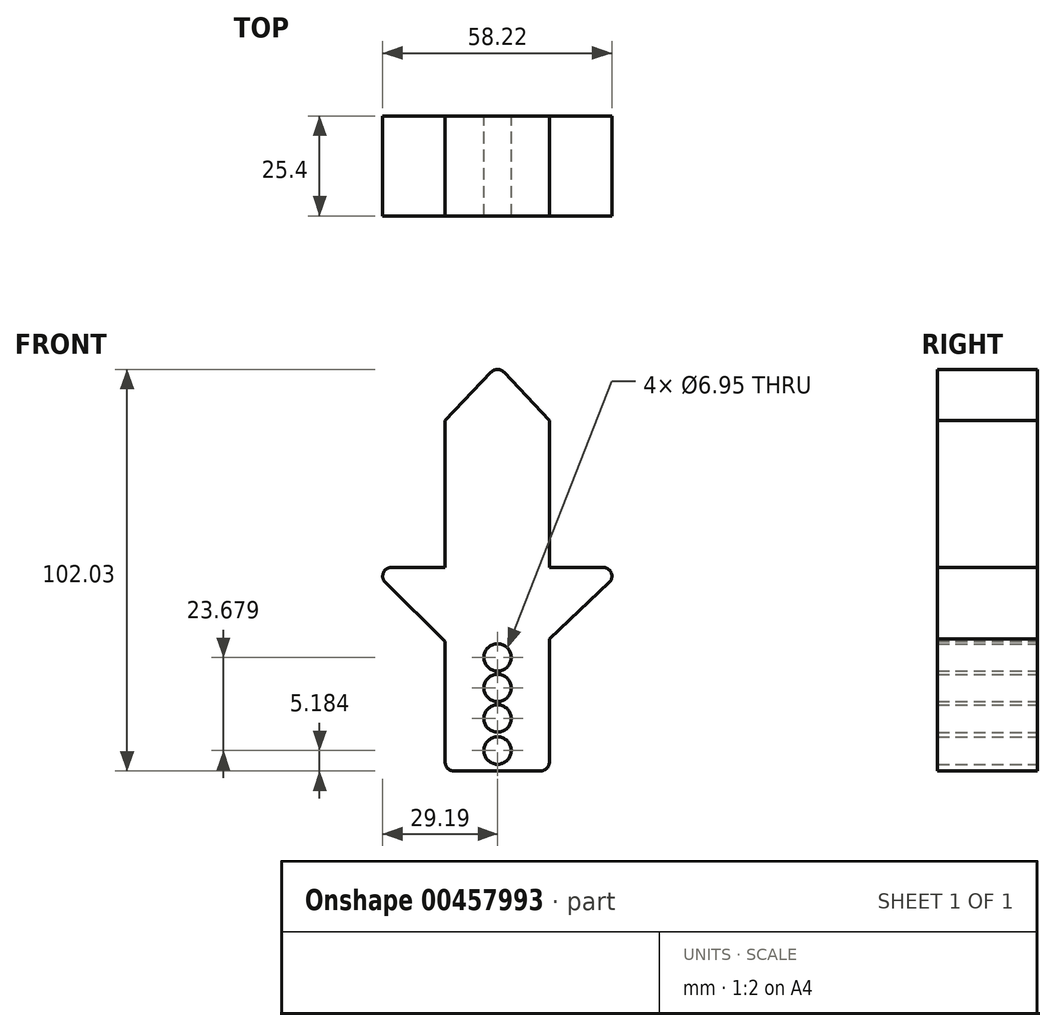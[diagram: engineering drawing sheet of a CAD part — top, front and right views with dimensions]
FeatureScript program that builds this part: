
annotation { "Feature Type Name" : "Feature", "Feature Type Description" : "" }
export const myFeature = defineFeature(function(context is Context, id is Id, definition is map)
    precondition{}
    {
        {
            var Q0;
            Q0=qCreatedBy(makeId("Front.planeOp"),FACE);
            var sketch = newSketch(context, id + "F0", { "sketchPlane" : qUnion([Q0])});
            skLineSegment(sketch, "E0", {"start": v(-13.32, 0) * mm, "end": v(-13.32, 37.28) * mm});
            skLineSegment(sketch, "E1", {"start": v(13.13, 37.28) * mm, "end": v(13.13, 0) * mm});
            skLineSegment(sketch, "E2", {"start": v(-13.32, 37.28) * mm, "end": v(0, 51.34) * mm});
            skLineSegment(sketch, "E3", {"start": v(13.13, 37.28) * mm, "end": v(0, 51.34) * mm});
            skLineSegment(sketch, "E4", {"start": v(-13.32, 0) * mm, "end": v(-32.37, 0) * mm});
            skLineSegment(sketch, "E5", {"start": v(-32.37, 0) * mm, "end": v(-13.32, -18.78) * mm});
            skLineSegment(sketch, "E6", {"start": v(13.13, 0) * mm, "end": v(32.37, 0) * mm});
            skLineSegment(sketch, "E7", {"start": v(32.37, 0) * mm, "end": v(13.13, -18.22) * mm});
            skLineSegment(sketch, "E8", {"start": v(-13.32, -18.78) * mm, "end": v(-13.32, -51.7) * mm});
            skLineSegment(sketch, "E9", {"start": v(-13.32, -51.7) * mm, "end": v(13.13, -51.7) * mm});
            skLineSegment(sketch, "E10", {"start": v(13.13, -18.22) * mm, "end": v(13.13, -51.7) * mm});
            skSolve(sketch);
        }
        {
            var Q0;
            Q0=makeQuery(id+"F0.imprint","IMPRINT",FACE,{"disambiguationData":[TD([[makeQuery(id+"F0.imprint","IMPRINT",EDGE,{"derivedFrom":sQuery(id+"F0.wireOp",EDGE,"E0")}),-1.0]])]});
            extrude(context, id + "F1", {"entities" : qUnion([Q0]), "depth" : 25.4 * mm});
        }
        {
            var Q0;
            Q0=qCreatedBy(makeId("Front.planeOp"),FACE);
            var sketch = newSketch(context, id + "F2", { "sketchPlane" : qUnion([Q0])});
            skCircle(sketch, "E11", {"center": v(0, -46.53) * mm, "radius": 3.48 * mm});
            skCircle(sketch, "E12", {"center": v(0, -38.39) * mm, "radius": 3.48 * mm});
            skCircle(sketch, "E13", {"center": v(0, -30.62) * mm, "radius": 3.48 * mm});
            skCircle(sketch, "E14", {"center": v(0, -22.85) * mm, "radius": 3.48 * mm});
            skSolve(sketch);
        }
        {
            var Q0;
            Q0=makeQuery(id+"F2.imprint","IMPRINT",FACE,{"disambiguationData":[TD([[makeQuery(id+"F2.imprint","IMPRINT",EDGE,{"derivedFrom":sQuery(id+"F2.wireOp",EDGE,"E14")}),1.0]])]});
            var Q1;
            Q1=makeQuery(id+"F2.imprint","IMPRINT",FACE,{"disambiguationData":[TD([[makeQuery(id+"F2.imprint","IMPRINT",EDGE,{"derivedFrom":sQuery(id+"F2.wireOp",EDGE,"E13")}),1.0]])]});
            var Q2;
            Q2=makeQuery(id+"F2.imprint","IMPRINT",FACE,{"disambiguationData":[TD([[makeQuery(id+"F2.imprint","IMPRINT",EDGE,{"derivedFrom":sQuery(id+"F2.wireOp",EDGE,"E12")}),1.0]])]});
            var Q3;
            Q3=makeQuery(id+"F2.imprint","IMPRINT",FACE,{"disambiguationData":[TD([[makeQuery(id+"F2.imprint","IMPRINT",EDGE,{"derivedFrom":sQuery(id+"F2.wireOp",EDGE,"E11")}),1.0]])]});
            var Q4;
            Q4=sQuery(id+"F2.wireOp",EDGE,"E14");
            var Q5;
            Q5=sQuery(id+"F2.wireOp",EDGE,"E13");
            var Q6;
            Q6=sQuery(id+"F2.wireOp",EDGE,"E12");
            var Q7;
            Q7=sQuery(id+"F2.wireOp",EDGE,"E11");
            extrude(context, id + "F3", {"entities" : qUnion([Q0, Q1, Q2, Q3]), "operationType" : NewBodyOperationType.REMOVE, "surfaceEntities" : qUnion([Q4, Q5, Q6, Q7]), "endBound" : BoundingType.THROUGH_ALL, "depth" : 50.8 * mm});
        }
        {
            var Q0;
            Q0=qCreatedBy(makeId("Front.planeOp"),FACE);
            var sketch = newSketch(context, id + "F4", { "sketchPlane" : qUnion([Q0])});
            skFitSpline(sketch, "E15", {"points": [v(-12.76, 37.1) * mm, v(-25.16, 39.5) * mm, v(-13.69, 40.6) * mm, v(-25.16, 49.3) * mm, v(-7.4, 45.79) * mm, v(-14.61, 60.4) * mm, v(-3.88, 53.74) * mm, v(0, 66.88) * mm, v(2.96, 53.56) * mm, v(13.5, 60.96) * mm, v(9.25, 47.45) * mm, v(19.05, 51.34) * mm, v(15.9, 41.9) * mm, v(26.08, 40.05) * mm, v(12.02, 37.1) * mm], "startDerivative": vector(-302.6, 50.45) * mm, "endDerivative": vector(-310.8, -58.33) * mm});
            skSolve(sketch);
        }
        {
            var Q0;
            Q0=sQuery(id+"F4.wireOp",EDGE,"E15");
            extrude(context, id + "F5", {"bodyType" : ToolBodyType.SURFACE, "operationType" : NewBodyOperationType.REMOVE, "surfaceEntities" : qUnion([Q0]), "depth" : 25.4 * mm});
        }
        {
            var Q0;
            Q0=makeQuery(id+"F1.opExtrude","SWEPT_EDGE",EDGE,{"disambiguationData":[OSD([sQuery(id+"F0.wireOp",EDGE,"E4"),sQuery(id+"F0.wireOp",EDGE,"E5")])]});
            var Q1;
            Q1=makeQuery(id+"F1.opExtrude","SWEPT_EDGE",EDGE,{"disambiguationData":[OSD([sQuery(id+"F0.wireOp",EDGE,"E6"),sQuery(id+"F0.wireOp",EDGE,"E7")])]});
            var Q2;
            Q2=makeQuery(id+"F1.opExtrude","SWEPT_EDGE",EDGE,{"disambiguationData":[OSD([sQuery(id+"F0.wireOp",EDGE,"E8"),sQuery(id+"F0.wireOp",EDGE,"E9")])]});
            var Q3;
            Q3=makeQuery(id+"F1.opExtrude","SWEPT_EDGE",EDGE,{"disambiguationData":[OSD([sQuery(id+"F0.wireOp",EDGE,"E9"),sQuery(id+"F0.wireOp",EDGE,"E10")])]});
            var Q4;
            Q4=makeQuery(id+"F1.opExtrude","SWEPT_EDGE",EDGE,{"disambiguationData":[OSD([sQuery(id+"F0.wireOp",EDGE,"E2"),sQuery(id+"F0.wireOp",EDGE,"E3")])]});
            fillet(context, id + "F6", {"entities" : qUnion([Q0, Q1, Q2, Q3, Q4]), "radius" : 2.2 * mm, "tangentPropagation" : true, "allowEdgeOverflow" : false});
        }
    });
